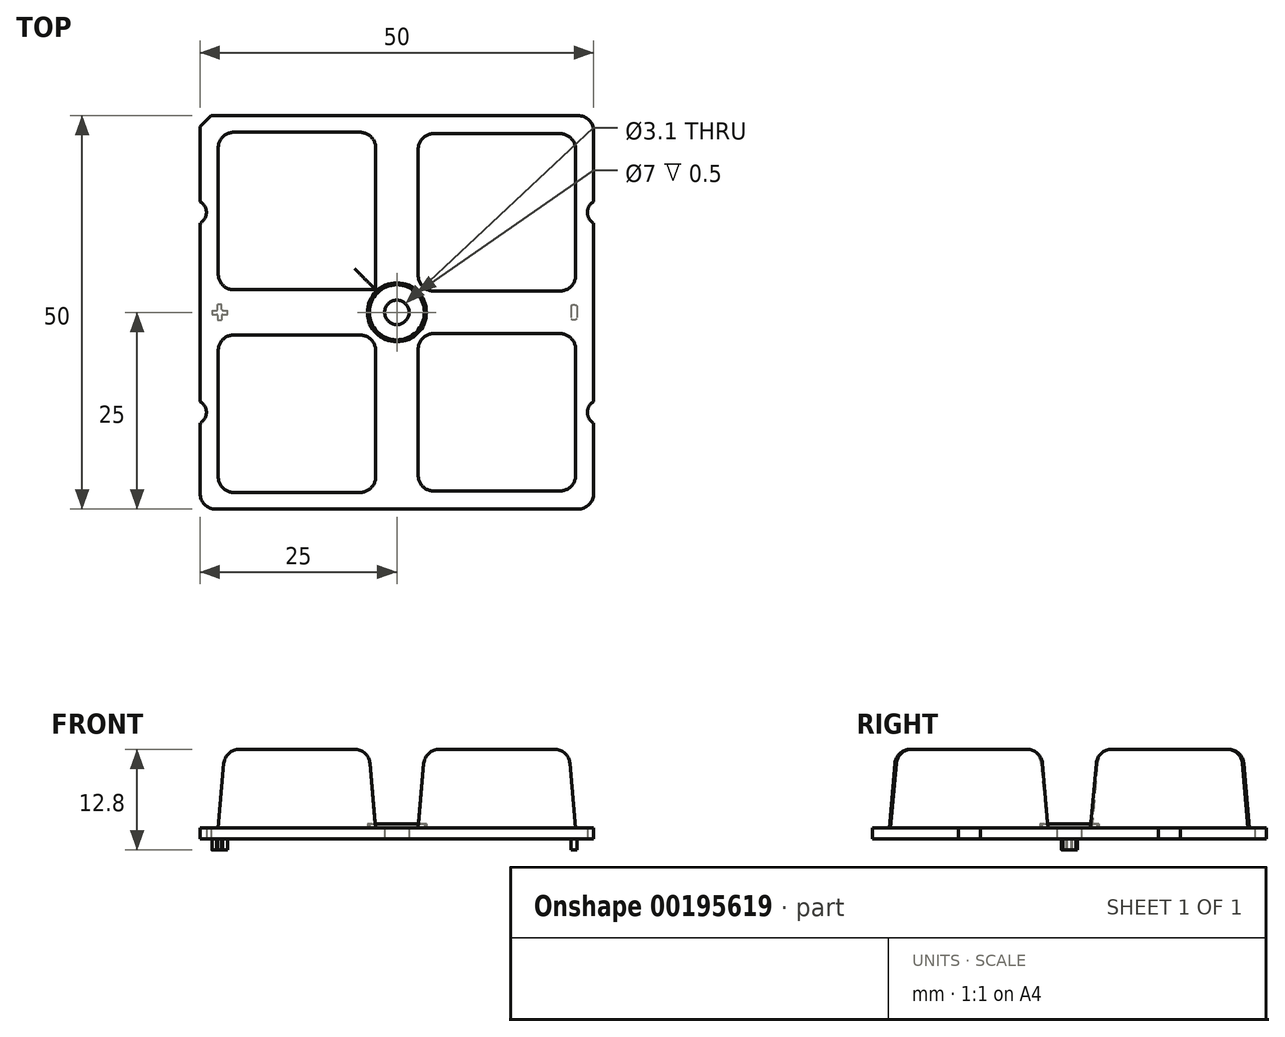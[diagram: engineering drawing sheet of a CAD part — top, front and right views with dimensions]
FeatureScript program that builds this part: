
annotation { "Feature Type Name" : "Feature", "Feature Type Description" : "" }
export const myFeature = defineFeature(function(context is Context, id is Id, definition is map)
    precondition{}
    {
        {
            var Q0;
            Q0=qCreatedBy(makeId("Top.planeOp"),FACE);
            var sketch = newSketch(context, id + "F0", { "sketchPlane" : qUnion([Q0])});
            skLineSegment(sketch, "E0.bottom", {"start": v(-23.59, 25) * mm, "end": v(23, 25) * mm});
            skLineSegment(sketch, "E0.top", {"start": v(-23, -25) * mm, "end": v(23, -25) * mm});
            skLineSegment(sketch, "E0.left", {"start": v(-25, 23.59) * mm, "end": v(-25, 14.09) * mm});
            skLineSegment(sketch, "E0.right", {"start": v(25, 23) * mm, "end": v(25, 14.09) * mm});
            skPoint(sketch, "E0.middle", {"position": v(0, 0) * mm});
            skLineSegment(sketch, "E1.bottom", {"start": v(-22.7, 2.87) * mm, "end": v(-2.7, 2.87) * mm, "construction": true});
            skLineSegment(sketch, "E1.top", {"start": v(-22.7, 22.87) * mm, "end": v(-2.7, 22.87) * mm, "construction": true});
            skLineSegment(sketch, "E1.left", {"start": v(-22.7, 2.87) * mm, "end": v(-22.7, 22.87) * mm, "construction": true});
            skLineSegment(sketch, "E1.right", {"start": v(-2.7, 2.87) * mm, "end": v(-2.7, 22.87) * mm, "construction": true});
            skPoint(sketch, "E1.middle", {"position": v(-12.7, 12.87) * mm});
            skLineSegment(sketch, "E2.bottom", {"start": v(2.7, 2.7) * mm, "end": v(22.7, 2.7) * mm, "construction": true});
            skLineSegment(sketch, "E2.top", {"start": v(2.7, 22.7) * mm, "end": v(22.7, 22.7) * mm, "construction": true});
            skLineSegment(sketch, "E2.left", {"start": v(2.7, 2.7) * mm, "end": v(2.7, 22.7) * mm, "construction": true});
            skLineSegment(sketch, "E2.right", {"start": v(22.7, 2.7) * mm, "end": v(22.7, 22.7) * mm, "construction": true});
            skPoint(sketch, "E2.middle", {"position": v(12.7, 12.7) * mm});
            skLineSegment(sketch, "E3.MirrorCS", {"start": v(-22.7, -2.87) * mm, "end": v(-2.7, -2.87) * mm, "construction": true});
            skLineSegment(sketch, "E4.MirrorCS", {"start": v(-22.7, -2.87) * mm, "end": v(-22.7, -22.87) * mm, "construction": true});
            skLineSegment(sketch, "E5.MirrorCS", {"start": v(-22.7, -22.87) * mm, "end": v(-2.7, -22.87) * mm, "construction": true});
            skLineSegment(sketch, "E6.MirrorCS", {"start": v(-2.7, -2.87) * mm, "end": v(-2.7, -22.87) * mm, "construction": true});
            skLineSegment(sketch, "E7.MirrorCS", {"start": v(2.7, -2.7) * mm, "end": v(2.7, -22.7) * mm, "construction": true});
            skLineSegment(sketch, "E8.MirrorCS", {"start": v(2.7, -22.7) * mm, "end": v(22.7, -22.7) * mm, "construction": true});
            skLineSegment(sketch, "E9.MirrorCS", {"start": v(2.7, -2.7) * mm, "end": v(22.7, -2.7) * mm, "construction": true});
            skLineSegment(sketch, "E10.MirrorCS", {"start": v(22.7, -2.7) * mm, "end": v(22.7, -22.7) * mm, "construction": true});
            skLineSegment(sketch, "E11", {"start": v(-25, 0) * mm, "end": v(25.8, 0) * mm, "construction": true});
            skPoint(sketch, "E11.endSnap0", {"position": v(25, 0) * mm});
            skLineSegment(sketch, "E12", {"start": v(25.8, 0) * mm, "end": v(25.8, 11.1) * mm, "construction": true});
            skArc(sketch, "E13", {"start": v(25, 14.09) * mm, "mid": v(24.2, 12.7) * mm, "end": v(25, 11.31) * mm});
            skArc(sketch, "E14.MirrorC", {"start": v(25, -14.09) * mm, "mid": v(24.2, -12.7) * mm, "end": v(25, -11.31) * mm});
            skLineSegment(sketch, "E15.trimOffspring", {"start": v(25, 11.31) * mm, "end": v(25, -11.31) * mm});
            skPoint(sketch, "E16.trimOffspring.end.orphan", {"position": v(25.8, 25.4) * mm});
            skLineSegment(sketch, "E17.trimOffspring", {"start": v(25, -14.09) * mm, "end": v(25, -23) * mm});
            skArc(sketch, "E18.MirrorCS", {"start": v(-25, 14.09) * mm, "mid": v(-24.2, 12.7) * mm, "end": v(-25, 11.31) * mm});
            skArc(sketch, "E19.MirrorCS", {"start": v(-25, -14.09) * mm, "mid": v(-24.2, -12.7) * mm, "end": v(-25, -11.31) * mm});
            skLineSegment(sketch, "E20.trimOffspring", {"start": v(-25, 11.31) * mm, "end": v(-25, -11.31) * mm});
            skLineSegment(sketch, "E21.trimOffspring", {"start": v(-25, -14.09) * mm, "end": v(-25, -23) * mm});
            skCircle(sketch, "E22", {"center": v(0, 0) * mm, "radius": 1.55 * mm});
            skPoint(sketch, "E23.visualSharp", {"position": v(25, 25) * mm});
            skArc(sketch, "E23.filletArc", {"start": v(25, 23) * mm, "mid": v(24.41, 24.41) * mm, "end": v(23, 25) * mm});
            skPoint(sketch, "E24.visualSharp", {"position": v(25, -25) * mm});
            skArc(sketch, "E24.filletArc", {"start": v(23, -25) * mm, "mid": v(24.41, -24.41) * mm, "end": v(25, -23) * mm});
            skPoint(sketch, "E25.visualSharp", {"position": v(-25, -25) * mm});
            skArc(sketch, "E25.filletArc", {"start": v(-25, -23) * mm, "mid": v(-24.41, -24.41) * mm, "end": v(-23, -25) * mm});
            skLineSegment(sketch, "E26", {"start": v(-25, 23.59) * mm, "end": v(-23.59, 25) * mm});
            skPoint(sketch, "E27.orphan", {"position": v(-25, 25) * mm});
            skSolve(sketch);
        }
        {
            var Q0;
            Q0=makeQuery(id+"F0.imprint","IMPRINT",FACE,{"disambiguationData":[TD([[makeQuery(id+"F0.imprint","IMPRINT",EDGE,{"derivedFrom":sQuery(id+"F0.wireOp",EDGE,"E0.bottom")}),-1.0]])]});
            var Q1;
            Q1=makeQuery(id+"F0.imprint","IMPRINT",FACE,{"disambiguationData":[TD([[makeQuery(id+"F0.imprint","IMPRINT",EDGE,{"derivedFrom":sQuery(id+"F0.wireOp",EDGE,"E22")}),-1.0]])]});
            extrude(context, id + "F1", {"entities" : qUnion([Q0, Q1]), "depth" : 1.4 * mm});
        }
        {
            var Q0;
            Q0=makeQuery(id+"F1.opExtrude","CAP_FACE",FACE,{"disambiguationData":[OSD([sQuery(id+"F0.wireOp",EDGE,"E0.bottom"),sQuery(id+"F0.wireOp",EDGE,"E0.top"),sQuery(id+"F0.wireOp",EDGE,"E0.left"),sQuery(id+"F0.wireOp",EDGE,"E0.right"),sQuery(id+"F0.wireOp",EDGE,"E1.bottom"),sQuery(id+"F0.wireOp",EDGE,"E1.top"),sQuery(id+"F0.wireOp",EDGE,"E1.left"),sQuery(id+"F0.wireOp",EDGE,"E1.right"),sQuery(id+"F0.wireOp",EDGE,"E2.bottom"),sQuery(id+"F0.wireOp",EDGE,"E2.top"),sQuery(id+"F0.wireOp",EDGE,"E2.left"),sQuery(id+"F0.wireOp",EDGE,"E2.right"),sQuery(id+"F0.wireOp",EDGE,"E3.MirrorCS"),sQuery(id+"F0.wireOp",EDGE,"E4.MirrorCS"),sQuery(id+"F0.wireOp",EDGE,"E5.MirrorCS"),sQuery(id+"F0.wireOp",EDGE,"E6.MirrorCS"),sQuery(id+"F0.wireOp",EDGE,"E7.MirrorCS"),sQuery(id+"F0.wireOp",EDGE,"E8.MirrorCS"),sQuery(id+"F0.wireOp",EDGE,"E9.MirrorCS"),sQuery(id+"F0.wireOp",EDGE,"E10.MirrorCS"),sQuery(id+"F0.wireOp",EDGE,"E13"),sQuery(id+"F0.wireOp",EDGE,"E14.MirrorC"),sQuery(id+"F0.wireOp",EDGE,"E15.trimOffspring"),sQuery(id+"F0.wireOp",EDGE,"E17.trimOffspring"),sQuery(id+"F0.wireOp",EDGE,"E18.MirrorCS"),sQuery(id+"F0.wireOp",EDGE,"E19.MirrorCS"),sQuery(id+"F0.wireOp",EDGE,"E20.trimOffspring"),sQuery(id+"F0.wireOp",EDGE,"E21.trimOffspring"),sQuery(id+"F0.wireOp",EDGE,"E22"),sQuery(id+"F0.wireOp",EDGE,"E23.filletArc"),sQuery(id+"F0.wireOp",EDGE,"E24.filletArc"),sQuery(id+"F0.wireOp",EDGE,"E25.filletArc"),sQuery(id+"F0.wireOp",EDGE,"E26")])],"isStart":false});
            var sketch = newSketch(context, id + "F2", { "sketchPlane" : qUnion([Q0])});
            skLineSegment(sketch, "E28.0", {"start": v(-2.7, 2.87) * mm, "end": v(-2.7, 22.87) * mm});
            skLineSegment(sketch, "E28.1", {"start": v(-22.7, 2.87) * mm, "end": v(-2.7, 2.87) * mm});
            skLineSegment(sketch, "E28.2", {"start": v(-22.7, 2.87) * mm, "end": v(-22.7, 22.87) * mm});
            skLineSegment(sketch, "E28.3", {"start": v(-22.7, 22.87) * mm, "end": v(-2.7, 22.87) * mm});
            skLineSegment(sketch, "E28.4", {"start": v(2.7, 22.7) * mm, "end": v(22.7, 22.7) * mm});
            skLineSegment(sketch, "E28.5", {"start": v(2.7, 2.7) * mm, "end": v(2.7, 22.7) * mm});
            skLineSegment(sketch, "E28.6", {"start": v(2.7, 2.7) * mm, "end": v(22.7, 2.7) * mm});
            skLineSegment(sketch, "E28.7", {"start": v(22.7, 2.7) * mm, "end": v(22.7, 22.7) * mm});
            skLineSegment(sketch, "E28.8", {"start": v(2.7, -2.7) * mm, "end": v(22.7, -2.7) * mm});
            skLineSegment(sketch, "E28.9", {"start": v(2.7, -2.7) * mm, "end": v(2.7, -22.7) * mm});
            skLineSegment(sketch, "E28.10", {"start": v(22.7, -2.7) * mm, "end": v(22.7, -22.7) * mm});
            skLineSegment(sketch, "E28.11", {"start": v(2.7, -22.7) * mm, "end": v(22.7, -22.7) * mm});
            skLineSegment(sketch, "E28.12", {"start": v(-22.7, -2.87) * mm, "end": v(-2.7, -2.87) * mm});
            skLineSegment(sketch, "E28.13", {"start": v(-2.7, -2.87) * mm, "end": v(-2.7, -22.87) * mm});
            skLineSegment(sketch, "E28.14", {"start": v(-22.7, -2.87) * mm, "end": v(-22.7, -22.87) * mm});
            skLineSegment(sketch, "E28.15", {"start": v(-22.7, -22.87) * mm, "end": v(-2.7, -22.87) * mm});
            skSolve(sketch);
        }
        {
            var Q0;
            Q0 = qSketchRegion(id + "F2", true);
            extrude(context, id + "F3", {"entities" : qUnion([Q0]), "operationType" : NewBodyOperationType.ADD, "depth" : 10 * mm, "hasDraft" : true, "draftAngle" : 5 * degree, "draftPullDirection" : true});
        }
        {
            var Q0;
            Q0=makeQuery(id+"F1.opExtrude","CAP_FACE",FACE,{"disambiguationData":[OSD([sQuery(id+"F0.wireOp",EDGE,"E0.bottom"),sQuery(id+"F0.wireOp",EDGE,"E0.top"),sQuery(id+"F0.wireOp",EDGE,"E0.left"),sQuery(id+"F0.wireOp",EDGE,"E0.right"),sQuery(id+"F0.wireOp",EDGE,"E1.bottom"),sQuery(id+"F0.wireOp",EDGE,"E1.top"),sQuery(id+"F0.wireOp",EDGE,"E1.left"),sQuery(id+"F0.wireOp",EDGE,"E1.right"),sQuery(id+"F0.wireOp",EDGE,"E2.bottom"),sQuery(id+"F0.wireOp",EDGE,"E2.top"),sQuery(id+"F0.wireOp",EDGE,"E2.left"),sQuery(id+"F0.wireOp",EDGE,"E2.right"),sQuery(id+"F0.wireOp",EDGE,"E3.MirrorCS"),sQuery(id+"F0.wireOp",EDGE,"E4.MirrorCS"),sQuery(id+"F0.wireOp",EDGE,"E5.MirrorCS"),sQuery(id+"F0.wireOp",EDGE,"E6.MirrorCS"),sQuery(id+"F0.wireOp",EDGE,"E7.MirrorCS"),sQuery(id+"F0.wireOp",EDGE,"E8.MirrorCS"),sQuery(id+"F0.wireOp",EDGE,"E9.MirrorCS"),sQuery(id+"F0.wireOp",EDGE,"E10.MirrorCS"),sQuery(id+"F0.wireOp",EDGE,"E13"),sQuery(id+"F0.wireOp",EDGE,"E14.MirrorC"),sQuery(id+"F0.wireOp",EDGE,"E15.trimOffspring"),sQuery(id+"F0.wireOp",EDGE,"E17.trimOffspring"),sQuery(id+"F0.wireOp",EDGE,"E18.MirrorCS"),sQuery(id+"F0.wireOp",EDGE,"E19.MirrorCS"),sQuery(id+"F0.wireOp",EDGE,"E20.trimOffspring"),sQuery(id+"F0.wireOp",EDGE,"E21.trimOffspring"),sQuery(id+"F0.wireOp",EDGE,"E22"),sQuery(id+"F0.wireOp",EDGE,"E23.filletArc"),sQuery(id+"F0.wireOp",EDGE,"E24.filletArc"),sQuery(id+"F0.wireOp",EDGE,"E25.filletArc"),sQuery(id+"F0.wireOp",EDGE,"E26")])],"isStart":false});
            var sketch = newSketch(context, id + "F4", { "sketchPlane" : qUnion([Q0])});
            skCircle(sketch, "E29", {"center": v(0, 0) * mm, "radius": 3.5 * mm});
            skCircle(sketch, "E30.0", {"center": v(0, 0) * mm, "radius": 3.75 * mm});
            skSolve(sketch);
        }
        {
            var Q0;
            Q0 = qSketchRegion(id + "F4", true);
            extrude(context, id + "F5", {"entities" : qUnion([Q0]), "operationType" : NewBodyOperationType.ADD, "depth" : .50 * mm});
        }
        {
            var Q0;
            Q0=makeQuery(id+"F1.opExtrude","CAP_FACE",FACE,{"disambiguationData":[OSD([sQuery(id+"F0.wireOp",EDGE,"E0.bottom"),sQuery(id+"F0.wireOp",EDGE,"E0.top"),sQuery(id+"F0.wireOp",EDGE,"E0.left"),sQuery(id+"F0.wireOp",EDGE,"E0.right"),sQuery(id+"F0.wireOp",EDGE,"E1.bottom"),sQuery(id+"F0.wireOp",EDGE,"E1.top"),sQuery(id+"F0.wireOp",EDGE,"E1.left"),sQuery(id+"F0.wireOp",EDGE,"E1.right"),sQuery(id+"F0.wireOp",EDGE,"E2.bottom"),sQuery(id+"F0.wireOp",EDGE,"E2.top"),sQuery(id+"F0.wireOp",EDGE,"E2.left"),sQuery(id+"F0.wireOp",EDGE,"E2.right"),sQuery(id+"F0.wireOp",EDGE,"E3.MirrorCS"),sQuery(id+"F0.wireOp",EDGE,"E4.MirrorCS"),sQuery(id+"F0.wireOp",EDGE,"E5.MirrorCS"),sQuery(id+"F0.wireOp",EDGE,"E6.MirrorCS"),sQuery(id+"F0.wireOp",EDGE,"E7.MirrorCS"),sQuery(id+"F0.wireOp",EDGE,"E8.MirrorCS"),sQuery(id+"F0.wireOp",EDGE,"E9.MirrorCS"),sQuery(id+"F0.wireOp",EDGE,"E10.MirrorCS"),sQuery(id+"F0.wireOp",EDGE,"E13"),sQuery(id+"F0.wireOp",EDGE,"E14.MirrorC"),sQuery(id+"F0.wireOp",EDGE,"E15.trimOffspring"),sQuery(id+"F0.wireOp",EDGE,"E17.trimOffspring"),sQuery(id+"F0.wireOp",EDGE,"E18.MirrorCS"),sQuery(id+"F0.wireOp",EDGE,"E19.MirrorCS"),sQuery(id+"F0.wireOp",EDGE,"E20.trimOffspring"),sQuery(id+"F0.wireOp",EDGE,"E21.trimOffspring"),sQuery(id+"F0.wireOp",EDGE,"E22"),sQuery(id+"F0.wireOp",EDGE,"E23.filletArc"),sQuery(id+"F0.wireOp",EDGE,"E24.filletArc"),sQuery(id+"F0.wireOp",EDGE,"E25.filletArc"),sQuery(id+"F0.wireOp",EDGE,"E26")])],"isStart":true});
            var sketch = newSketch(context, id + "F6", { "sketchPlane" : qUnion([Q0])});
            skLineSegment(sketch, "E31", {"start": v(-22.75, 0) * mm, "end": v(-22.25, 0) * mm, "construction": true});
            skArc(sketch, "E32", {"start": v(-23.47, 0.25) * mm, "mid": v(-23.5, 0) * mm, "end": v(-23.47, -0.25) * mm});
            skCircle(sketch, "E33", {"center": v(22.5, 0) * mm, "radius": 1 * mm, "construction": true});
            skLineSegment(sketch, "E34.left", {"start": v(22.12, -0.83) * mm, "end": v(22.12, 0.83) * mm});
            skLineSegment(sketch, "E34.right", {"start": v(22.88, -0.8) * mm, "end": v(22.88, 0.8) * mm});
            skCircle(sketch, "E35", {"center": v(22.5, 0) * mm, "radius": 0.35 * mm, "construction": true});
            skArc(sketch, "E36", {"start": v(22.88, 0.8) * mm, "mid": v(22.5, 0.92) * mm, "end": v(22.12, 0.83) * mm});
            skArc(sketch, "E37.MirrorCS", {"start": v(22.88, -0.8) * mm, "mid": v(22.5, -0.92) * mm, "end": v(22.12, -0.83) * mm});
            skPoint(sketch, "E34.top.start.orphan", {"position": v(22.12, 0.92) * mm});
            skPoint(sketch, "E38.orphan", {"position": v(22.88, 0.92) * mm});
            skPoint(sketch, "E39.orphan", {"position": v(22.12, -0.92) * mm});
            skPoint(sketch, "E40.orphan", {"position": v(22.88, -0.92) * mm});
            skLineSegment(sketch, "E41", {"start": v(-22.5, 0.25) * mm, "end": v(-22.5, 1) * mm, "construction": true});
            skLineSegment(sketch, "E42", {"start": v(-22.5, 0) * mm, "end": v(-22.5, -1) * mm, "construction": true});
            skLineSegment(sketch, "E43.0", {"start": v(-22.25, 0.38) * mm, "end": v(-22.25, 0.97) * mm});
            skLineSegment(sketch, "E44.0", {"start": v(-22.75, 0.38) * mm, "end": v(-22.75, 0.97) * mm});
            skLineSegment(sketch, "E45.0", {"start": v(-22.75, -0.38) * mm, "end": v(-22.75, -0.97) * mm});
            skLineSegment(sketch, "E46.0", {"start": v(-22.25, -0.38) * mm, "end": v(-22.25, -0.97) * mm});
            skLineSegment(sketch, "E47.trimOffspring", {"start": v(21.5, 0) * mm, "end": v(25, 0) * mm, "construction": true});
            skPoint(sketch, "E48.orphan", {"position": v(-25, 0) * mm});
            skLineSegment(sketch, "E49.0", {"start": v(-23.47, -0.25) * mm, "end": v(-22.88, -0.25) * mm});
            skLineSegment(sketch, "E50.0", {"start": v(-23.47, 0.25) * mm, "end": v(-22.88, 0.25) * mm});
            skLineSegment(sketch, "E51.trimOffspring", {"start": v(-22.12, -0.25) * mm, "end": v(-21.53, -0.25) * mm});
            skLineSegment(sketch, "E52.trimOffspring", {"start": v(-22.12, 0.25) * mm, "end": v(-21.53, 0.25) * mm});
            skArc(sketch, "E53", {"start": v(-22.88, 0.25) * mm, "mid": v(-22.78, 0.3) * mm, "end": v(-22.75, 0.42) * mm});
            skArc(sketch, "E54.MirrorCS", {"start": v(-22.12, 0.25) * mm, "mid": v(-22.22, 0.3) * mm, "end": v(-22.25, 0.42) * mm});
            skArc(sketch, "E55.MirrorCS", {"start": v(-22.88, -0.25) * mm, "mid": v(-22.78, -0.3) * mm, "end": v(-22.75, -0.42) * mm});
            skArc(sketch, "E56.MirrorCS", {"start": v(-22.12, -0.25) * mm, "mid": v(-22.22, -0.3) * mm, "end": v(-22.25, -0.42) * mm});
            skArc(sketch, "E57.trimOffspring", {"start": v(-22.25, 0.97) * mm, "mid": v(-22.5, 1) * mm, "end": v(-22.75, 0.97) * mm});
            skArc(sketch, "E58.trimOffspring", {"start": v(-21.53, -0.25) * mm, "mid": v(-21.5, 0) * mm, "end": v(-21.53, 0.25) * mm});
            skArc(sketch, "E59.trimOffspring", {"start": v(-22.75, -0.97) * mm, "mid": v(-22.5, -1) * mm, "end": v(-22.25, -0.97) * mm});
            skSolve(sketch);
        }
        {
            var Q0;
            Q0 = qSketchRegion(id + "F6", true);
            extrude(context, id + "F7", {"entities" : qUnion([Q0]), "operationType" : NewBodyOperationType.ADD, "depth" : 1.4 * mm});
        }
        {
            var Q0;
            Q0=makeQuery(id+"F3.opExtrude","CAP_FACE",FACE,{"disambiguationData":[OSD([sQuery(id+"F2.wireOp",EDGE,"E28.0"),sQuery(id+"F2.wireOp",EDGE,"E28.1"),sQuery(id+"F2.wireOp",EDGE,"E28.2"),sQuery(id+"F2.wireOp",EDGE,"E28.3")])],"isStart":false});
            var Q1;
            Q1=makeQuery(id+"F3.opExtrude","CAP_FACE",FACE,{"disambiguationData":[OSD([sQuery(id+"F2.wireOp",EDGE,"E28.4"),sQuery(id+"F2.wireOp",EDGE,"E28.5"),sQuery(id+"F2.wireOp",EDGE,"E28.7"),sQuery(id+"F2.wireOp",EDGE,"E28.6")])],"isStart":false});
            var Q2;
            Q2=makeQuery(id+"F3.opExtrude","CAP_FACE",FACE,{"disambiguationData":[OSD([sQuery(id+"F2.wireOp",EDGE,"E28.8"),sQuery(id+"F2.wireOp",EDGE,"E28.9"),sQuery(id+"F2.wireOp",EDGE,"E28.10"),sQuery(id+"F2.wireOp",EDGE,"E28.11")])],"isStart":false});
            var Q3;
            Q3=makeQuery(id+"F3.opExtrude","CAP_FACE",FACE,{"disambiguationData":[OSD([sQuery(id+"F2.wireOp",EDGE,"E28.12"),sQuery(id+"F2.wireOp",EDGE,"E28.13"),sQuery(id+"F2.wireOp",EDGE,"E28.14"),sQuery(id+"F2.wireOp",EDGE,"E28.15")])],"isStart":false});
            var Q4;
            Q4=makeQuery(id+"F3.opExtrude","SWEPT_EDGE",EDGE,{"disambiguationData":[OSD([sQuery(id+"F2.wireOp",EDGE,"E28.1"),sQuery(id+"F2.wireOp",EDGE,"E28.2")])]});
            var Q5;
            Q5=makeQuery(id+"F3.opExtrude","SWEPT_EDGE",EDGE,{"disambiguationData":[OSD([sQuery(id+"F2.wireOp",EDGE,"E28.12"),sQuery(id+"F2.wireOp",EDGE,"E28.14")])]});
            var Q6;
            Q6=makeQuery(id+"F3.opExtrude","SWEPT_EDGE",EDGE,{"disambiguationData":[OSD([sQuery(id+"F2.wireOp",EDGE,"E28.14"),sQuery(id+"F2.wireOp",EDGE,"E28.15")])]});
            var Q7;
            Q7=makeQuery(id+"F3.opExtrude","SWEPT_EDGE",EDGE,{"disambiguationData":[OSD([sQuery(id+"F2.wireOp",EDGE,"E28.13"),sQuery(id+"F2.wireOp",EDGE,"E28.15")])]});
            var Q8;
            Q8=makeQuery(id+"F3.opExtrude","SWEPT_EDGE",EDGE,{"disambiguationData":[OSD([sQuery(id+"F2.wireOp",EDGE,"E28.9"),sQuery(id+"F2.wireOp",EDGE,"E28.11")])]});
            var Q9;
            Q9=makeQuery(id+"F3.opExtrude","SWEPT_EDGE",EDGE,{"disambiguationData":[OSD([sQuery(id+"F2.wireOp",EDGE,"E28.10"),sQuery(id+"F2.wireOp",EDGE,"E28.11")])]});
            var Q10;
            Q10=makeQuery(id+"F3.opExtrude","SWEPT_EDGE",EDGE,{"disambiguationData":[OSD([sQuery(id+"F2.wireOp",EDGE,"E28.5"),sQuery(id+"F2.wireOp",EDGE,"E28.6")])]});
            var Q11;
            Q11=makeQuery(id+"F3.opExtrude","SWEPT_EDGE",EDGE,{"disambiguationData":[OSD([sQuery(id+"F2.wireOp",EDGE,"E28.7"),sQuery(id+"F2.wireOp",EDGE,"E28.6")])]});
            var Q12;
            Q12=makeQuery(id+"F3.opExtrude","SWEPT_EDGE",EDGE,{"disambiguationData":[OSD([sQuery(id+"F2.wireOp",EDGE,"E28.4"),sQuery(id+"F2.wireOp",EDGE,"E28.7")])]});
            var Q13;
            Q13=makeQuery(id+"F3.opExtrude","SWEPT_EDGE",EDGE,{"disambiguationData":[OSD([sQuery(id+"F2.wireOp",EDGE,"E28.4"),sQuery(id+"F2.wireOp",EDGE,"E28.5")])]});
            var Q14;
            Q14=makeQuery(id+"F3.opExtrude","SWEPT_EDGE",EDGE,{"disambiguationData":[OSD([sQuery(id+"F2.wireOp",EDGE,"E28.0"),sQuery(id+"F2.wireOp",EDGE,"E28.3")])]});
            var Q15;
            Q15=makeQuery(id+"F3.opExtrude","SWEPT_EDGE",EDGE,{"disambiguationData":[OSD([sQuery(id+"F2.wireOp",EDGE,"E28.2"),sQuery(id+"F2.wireOp",EDGE,"E28.3")])]});
            var Q16;
            Q16=makeQuery(id+"F3.opExtrude","SWEPT_EDGE",EDGE,{"disambiguationData":[OSD([sQuery(id+"F2.wireOp",EDGE,"E28.8"),sQuery(id+"F2.wireOp",EDGE,"E28.10")])]});
            var Q17;
            Q17=makeQuery(id+"F3.opExtrude","SWEPT_EDGE",EDGE,{"disambiguationData":[OSD([sQuery(id+"F2.wireOp",EDGE,"E28.8"),sQuery(id+"F2.wireOp",EDGE,"E28.9")])]});
            var Q18;
            Q18=makeQuery(id+"F3.opExtrude","SWEPT_EDGE",EDGE,{"disambiguationData":[OSD([sQuery(id+"F2.wireOp",EDGE,"E28.12"),sQuery(id+"F2.wireOp",EDGE,"E28.13")])]});
            fillet(context, id + "F8", {"entities" : qUnion([Q0, Q1, Q2, Q3, Q4, Q5, Q6, Q7, Q8, Q9, Q10, Q11, Q12, Q13, Q14, Q15, Q16, Q17, Q18]), "radius" : 2 * mm, "tangentPropagation" : true, "allowEdgeOverflow" : false});
        }
    });
